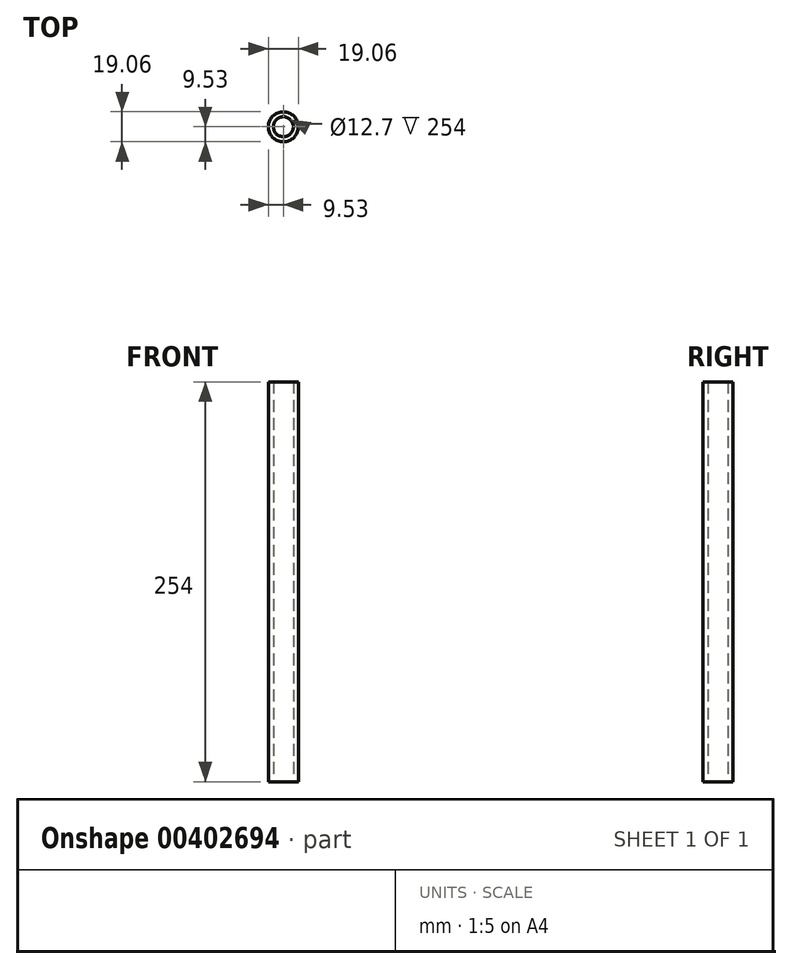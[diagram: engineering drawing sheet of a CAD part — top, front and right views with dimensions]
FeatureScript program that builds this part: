
annotation { "Feature Type Name" : "Feature", "Feature Type Description" : "" }
export const myFeature = defineFeature(function(context is Context, id is Id, definition is map)
    precondition{}
    {
        {
            var Q0;
            Q0=qCreatedBy(makeId("Top.planeOp"),FACE);
            var sketch = newSketch(context, id + "F0", { "sketchPlane" : qUnion([Q0])});
            skCircle(sketch, "E0", {"center": v(0, 0) * mm, "radius": 9.53 * mm});
            skCircle(sketch, "E1", {"center": v(0, 0) * mm, "radius": 6.35 * mm});
            skSolve(sketch);
        }
        {
            var Q0;
            Q0=makeQuery(id+"F0.imprint","IMPRINT",FACE,{"disambiguationData":[TD([[makeQuery(id+"F0.imprint","IMPRINT",EDGE,{"derivedFrom":sQuery(id+"F0.wireOp",EDGE,"E0")}),1.0]])]});
            extrude(context, id + "F1", {"entities" : qUnion([Q0]), "depth" : 254 * mm, "offsetDistance" : 25.4 * mm});
        }
    });
